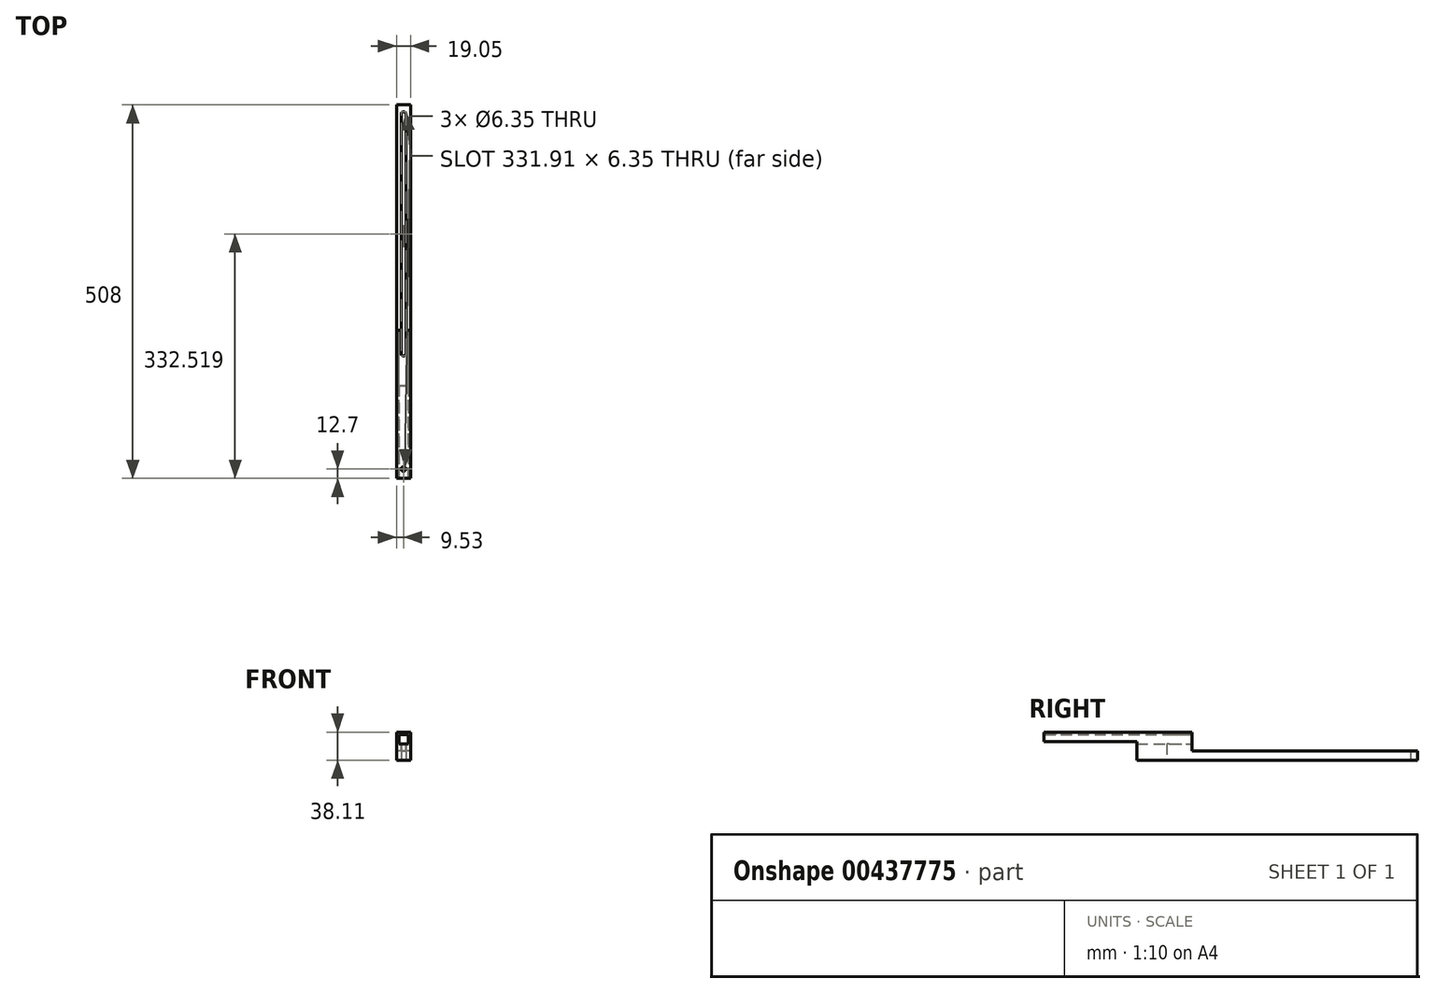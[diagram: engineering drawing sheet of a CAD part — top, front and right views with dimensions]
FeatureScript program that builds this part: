
annotation { "Feature Type Name" : "Feature", "Feature Type Description" : "" }
export const myFeature = defineFeature(function(context is Context, id is Id, definition is map)
    precondition{}
    {
        {
            var Q0;
            Q0=qCreatedBy(makeId("Front.planeOp"),FACE);
            var sketch = newSketch(context, id + "F0", { "sketchPlane" : qUnion([Q0])});
            skLineSegment(sketch, "E0.bottom", {"start": v(-15.88, 15.88) * mm, "end": v(3.17, 15.88) * mm});
            skLineSegment(sketch, "E0.top", {"start": v(-15.87, -22.23) * mm, "end": v(3.18, -22.23) * mm});
            skLineSegment(sketch, "E0.left", {"start": v(-15.88, 15.88) * mm, "end": v(-15.87, -22.22) * mm});
            skLineSegment(sketch, "E0.right", {"start": v(3.17, 15.88) * mm, "end": v(3.18, -22.23) * mm});
            skLineSegment(sketch, "E1.bottom", {"start": v(-12.7, 12.7) * mm, "end": v(0, 12.7) * mm});
            skLineSegment(sketch, "E1.top", {"start": v(-12.7, 0) * mm, "end": v(0, 0) * mm});
            skLineSegment(sketch, "E1.left", {"start": v(-12.7, 12.7) * mm, "end": v(-12.7, 0) * mm});
            skLineSegment(sketch, "E1.right", {"start": v(0, 12.7) * mm, "end": v(0, 0) * mm});
            skSolve(sketch);
        }
        {
            var Q0;
            Q0=qSketchRegion(id+"F0",true);
            extrude(context, id + "F1", {"entities" : qUnion([Q0]), "depth" : 508 * mm});
        }
        {
            var Q0;
            Q0=qCreatedBy(makeId("Top.planeOp"),FACE);
            var sketch = newSketch(context, id + "F2", { "sketchPlane" : qUnion([Q0])});
            skArc(sketch, "E2", {"start": v(-3.18, -12.7) * mm, "mid": v(-6.35, -9.52) * mm, "end": v(-9.52, -12.7) * mm});
            skLineSegment(sketch, "E3", {"start": v(-9.53, -12.7) * mm, "end": v(-9.53, -254) * mm});
            skLineSegment(sketch, "E4", {"start": v(-3.18, -12.7) * mm, "end": v(-3.18, -254) * mm});
            skPoint(sketch, "E5.center.orphan", {"position": v(-6.35, -254) * mm});
            skCircle(sketch, "E6", {"center": v(-6.35, -495.3) * mm, "radius": 3.18 * mm});
            skPoint(sketch, "E7.start.orphan", {"position": v(-9.52, -495.3) * mm});
            skPoint(sketch, "E8.endSnap0", {"position": v(-6.35, -257.18) * mm});
            skArc(sketch, "E9", {"start": v(-9.53, -338.26) * mm, "mid": v(-6.35, -341.44) * mm, "end": v(-3.18, -338.26) * mm});
            skLineSegment(sketch, "E10", {"start": v(-3.18, -254) * mm, "end": v(-3.18, -338.26) * mm});
            skLineSegment(sketch, "E11", {"start": v(-9.53, -254) * mm, "end": v(-9.53, -338.26) * mm});
            skSolve(sketch);
        }
        {
            var Q0;
            Q0=qSketchRegion(id+"F2",true);
            extrude(context, id + "F3", {"entities" : qUnion([Q0]), "operationType" : NewBodyOperationType.REMOVE, "depth" : 127 * mm, "symmetric" : true});
        }
        {
            var Q0;
            Q0=makeQuery(id+"F1.opExtrude","SWEPT_FACE",FACE,{"disambiguationData":[OSD([sQuery(id+"F0.wireOp",EDGE,"E0.left")])]});
            var sketch = newSketch(context, id + "F4", { "sketchPlane" : qUnion([Q0])});
            skLineSegment(sketch, "E12.bottom", {"start": v(0, 15.88) * mm, "end": v(306.72, 15.88) * mm});
            skLineSegment(sketch, "E12.top", {"start": v(0, -9.53) * mm, "end": v(306.72, -9.53) * mm});
            skLineSegment(sketch, "E12.left", {"start": v(0, 15.88) * mm, "end": v(0, -9.53) * mm});
            skLineSegment(sketch, "E12.right", {"start": v(306.72, 15.88) * mm, "end": v(306.72, -9.53) * mm});
            skLineSegment(sketch, "E13.bottom", {"start": v(508, -22.22) * mm, "end": v(381.84, -22.22) * mm});
            skLineSegment(sketch, "E13.top", {"start": v(508, 3.18) * mm, "end": v(381.84, 3.17) * mm});
            skLineSegment(sketch, "E13.left", {"start": v(508, -22.22) * mm, "end": v(508, 3.18) * mm});
            skLineSegment(sketch, "E13.right", {"start": v(381.84, -22.22) * mm, "end": v(381.84, 3.17) * mm});
            skSolve(sketch);
        }
        {
            var Q0;
            Q0 = qSketchRegion(id + "F4", true);
            extrude(context, id + "F5", {"entities" : qUnion([Q0]), "operationType" : NewBodyOperationType.REMOVE, "oppositeDirection" : true, "depth" : 25.4 * mm});
        }
    });
